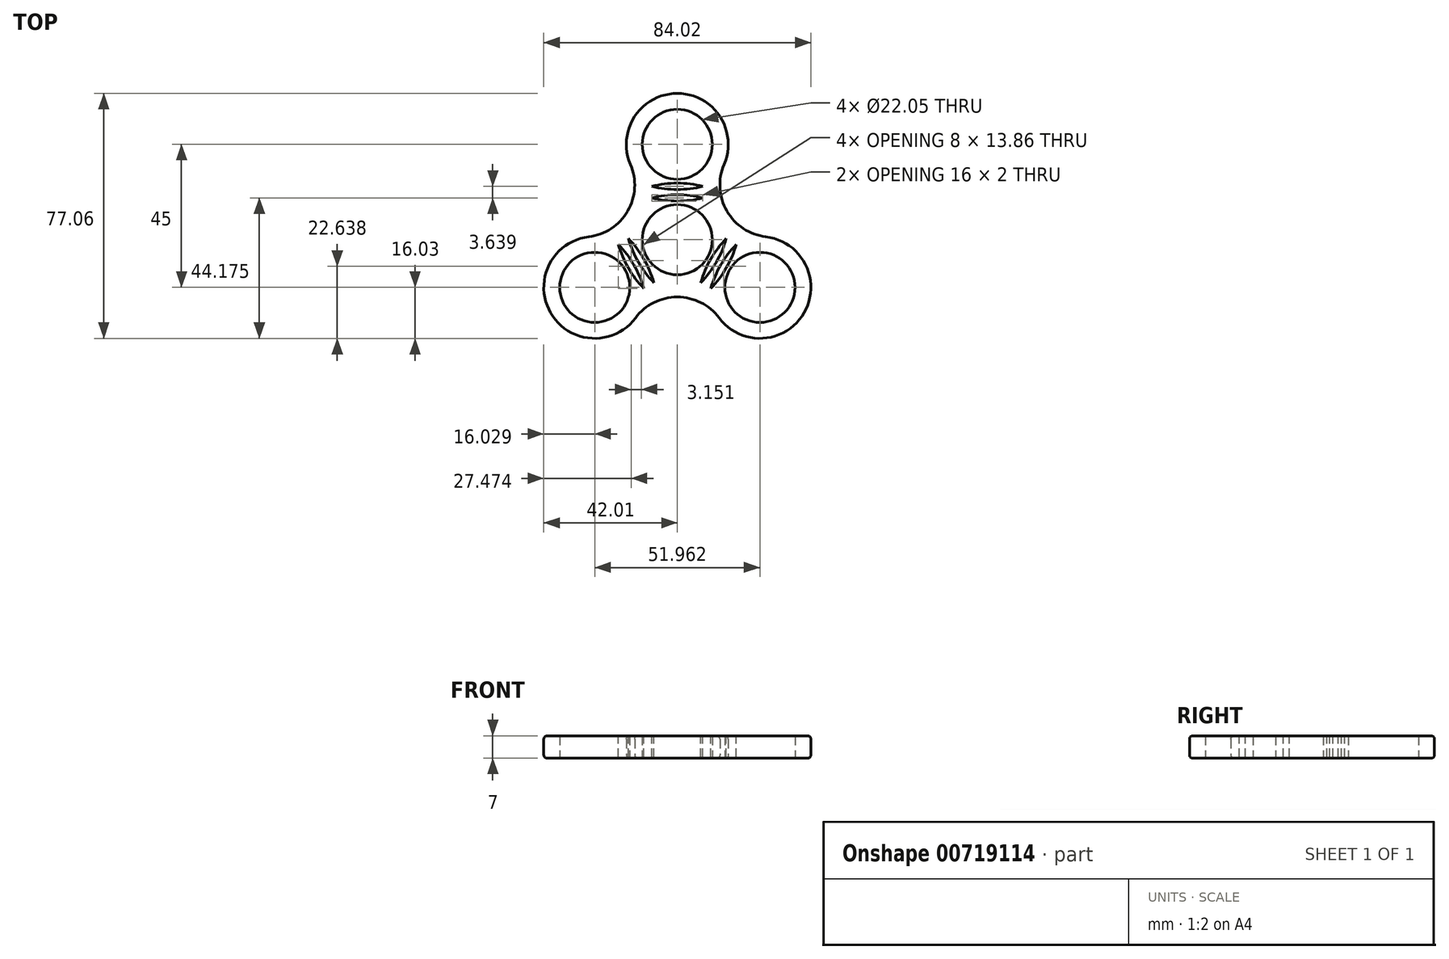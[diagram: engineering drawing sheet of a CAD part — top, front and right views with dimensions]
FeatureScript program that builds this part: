
annotation { "Feature Type Name" : "Feature", "Feature Type Description" : "" }
export const myFeature = defineFeature(function(context is Context, id is Id, definition is map)
    precondition{}
    {
        {
            var Q0;
            Q0=qCreatedBy(makeId("Top.planeOp"),FACE);
            var sketch = newSketch(context, id + "F0", { "sketchPlane" : qUnion([Q0])});
            skCircle(sketch, "E0", {"center": v(0, 0) * mm, "radius": 11.03 * mm});
            skCircle(sketch, "E1", {"center": v(0, 30) * mm, "radius": 11.03 * mm});
            skCircle(sketch, "E2.0", {"center": v(0, 30) * mm, "radius": 16.02 * mm});
            skCircle(sketch, "E3.0", {"center": v(0, 0) * mm, "radius": 18.02 * mm});
            skArc(sketch, "E4", {"start": v(-15.59, 9.05) * mm, "mid": v(-13.42, 16.25) * mm, "end": v(-14.72, 23.66) * mm});
            skLineSegment(sketch, "E5", {"start": v(0, -22.67) * mm, "end": v(0, 73.3) * mm, "construction": true});
            skArc(sketch, "E6.MirrorCS", {"start": v(15.59, 9.05) * mm, "mid": v(13.42, 16.25) * mm, "end": v(14.72, 23.66) * mm});
            skArc(sketch, "E7.1.0", {"start": v(-0.04, -18.02) * mm, "mid": v(-7.36, -19.75) * mm, "end": v(-13.13, -24.58) * mm});
            skArc(sketch, "E7.1.1", {"start": v(-15.63, 8.98) * mm, "mid": v(-20.78, 3.5) * mm, "end": v(-27.85, 0.92) * mm});
            skCircle(sketch, "E7.1.2", {"center": v(-25.98, -15) * mm, "radius": 16.02 * mm});
            skCircle(sketch, "E7.1.3", {"center": v(-25.98, -15) * mm, "radius": 11.03 * mm});
            skArc(sketch, "E7.2.0", {"start": v(15.63, 8.98) * mm, "mid": v(20.78, 3.5) * mm, "end": v(27.85, 0.92) * mm});
            skArc(sketch, "E7.2.1", {"start": v(0.04, -18.02) * mm, "mid": v(7.36, -19.75) * mm, "end": v(13.13, -24.58) * mm});
            skCircle(sketch, "E7.2.2", {"center": v(25.98, -15) * mm, "radius": 16.02 * mm});
            skCircle(sketch, "E7.2.3", {"center": v(25.98, -15) * mm, "radius": 11.03 * mm});
            skSolve(sketch);
        }
        {
            var Q0;
            Q0=qSketchRegion(id+"F0",true);
            var Q1;
            Q1=makeQuery(id+"F0.imprint","IMPRINT",FACE,{"disambiguationData":[TD([[makeQuery(id+"F0.imprint","IMPRINT",EDGE,{"derivedFrom":sQuery(id+"F0.wireOp",EDGE,"E0")}),-1.0]])]});
            var Q2;
            {var subQ0=sQuery(id+"F0.wireOp",EDGE,"E7.1.2");var subQ1=sQuery(id+"F0.wireOp",EDGE,"E3.0");var subQ2=makeQuery(id+"F0.imprint","INTERSECT",VERTEX,{"disambiguationData":[OD(0.0)],"derivedFrom":[subQ1,subQ0]});Q2=makeQuery(id+"F0.imprint","IMPRINT",FACE,{"disambiguationData":[TD([[makeQuery(id+"F0.imprint","IMPRINT",EDGE,{"disambiguationData":[TD([[subQ2,-1.0]])],"derivedFrom":subQ1}),1.0]])]});}
            var Q3;
            {var subQ0=sQuery(id+"F0.wireOp",EDGE,"E3.0");var subQ1=sQuery(id+"F0.wireOp",EDGE,"E2.0");var subQ2=makeQuery(id+"F0.imprint","INTERSECT",VERTEX,{"disambiguationData":[OD(0.0)],"derivedFrom":[subQ1,subQ0]});Q3=makeQuery(id+"F0.imprint","IMPRINT",FACE,{"disambiguationData":[TD([[makeQuery(id+"F0.imprint","IMPRINT",EDGE,{"disambiguationData":[TD([[subQ2,-1.0]])],"derivedFrom":subQ1}),1.0]])]});}
            var Q4;
            {var subQ0=sQuery(id+"F0.wireOp",EDGE,"E7.2.2");var subQ1=sQuery(id+"F0.wireOp",EDGE,"E3.0");var subQ2=makeQuery(id+"F0.imprint","INTERSECT",VERTEX,{"disambiguationData":[OD(0.0)],"derivedFrom":[subQ1,subQ0]});Q4=makeQuery(id+"F0.imprint","IMPRINT",FACE,{"disambiguationData":[TD([[makeQuery(id+"F0.imprint","IMPRINT",EDGE,{"disambiguationData":[TD([[subQ2,-1.0]])],"derivedFrom":subQ1}),1.0]])]});}
            extrude(context, id + "F1", {"entities" : qUnion([Q0, Q1, Q2, Q3, Q4]), "depth" : 7 * mm, "offsetDistance" : 25 * mm});
        }
        {
            var Q0;
            Q0=makeQuery(id+"F1.opExtrude","SWEPT_FACE",FACE,{"disambiguationData":[OSD([sQuery(id+"F0.wireOp",EDGE,"E2.0")])]});
            var Q1;
            Q1=makeQuery(id+"F1.opExtrude","SWEPT_FACE",FACE,{"disambiguationData":[OSD([sQuery(id+"F0.wireOp",EDGE,"E4")])]});
            var Q2;
            Q2=makeQuery(id+"F1.opExtrude","SWEPT_FACE",FACE,{"disambiguationData":[OSD([sQuery(id+"F0.wireOp",EDGE,"E7.1.1")])]});
            var Q3;
            Q3=makeQuery(id+"F1.opExtrude","SWEPT_FACE",FACE,{"disambiguationData":[OSD([sQuery(id+"F0.wireOp",EDGE,"E7.1.2")])]});
            var Q4;
            Q4=makeQuery(id+"F1.opExtrude","SWEPT_FACE",FACE,{"disambiguationData":[OSD([sQuery(id+"F0.wireOp",EDGE,"E7.2.1")])]});
            fillet(context, id + "F2", {"entities" : qUnion([Q0, Q1, Q2, Q3, Q4]), "radius" : 1 * mm, "tangentPropagation" : true, "allowEdgeOverflow" : false});
        }
        {
            var Q0;
            Q0=makeQuery(id+"F1.opExtrude","CAP_FACE",FACE,{"disambiguationData":[OSD([sQuery(id+"F0.wireOp",EDGE,"E0"),sQuery(id+"F0.wireOp",EDGE,"E1"),sQuery(id+"F0.wireOp",EDGE,"E2.0"),sQuery(id+"F0.wireOp",EDGE,"E3.0"),sQuery(id+"F0.wireOp",EDGE,"E4"),sQuery(id+"F0.wireOp",EDGE,"E6.MirrorCS"),sQuery(id+"F0.wireOp",EDGE,"E7.1.0"),sQuery(id+"F0.wireOp",EDGE,"E7.1.1"),sQuery(id+"F0.wireOp",EDGE,"E7.1.2"),sQuery(id+"F0.wireOp",EDGE,"E7.1.3"),sQuery(id+"F0.wireOp",EDGE,"E7.2.0"),sQuery(id+"F0.wireOp",EDGE,"E7.2.1"),sQuery(id+"F0.wireOp",EDGE,"E7.2.2"),sQuery(id+"F0.wireOp",EDGE,"E7.2.3")])],"isStart":false});
            var sketch = newSketch(context, id + "F3", { "sketchPlane" : qUnion([Q0])});
            skArc(sketch, "E8", {"start": v(8, 16.78) * mm, "mid": v(0, 17.78) * mm, "end": v(-8, 16.78) * mm});
            skArc(sketch, "E9", {"start": v(-8, 16.78) * mm, "mid": v(0, 15.79) * mm, "end": v(8, 16.78) * mm});
            skLineSegment(sketch, "E10", {"start": v(0, 48.36) * mm, "end": v(0, -14.8) * mm, "construction": true});
            skPoint(sketch, "E11", {"position": v(0, 17.78) * mm});
            skLineSegment(sketch, "E12", {"start": v(-8, 16.78) * mm, "end": v(-8, 48.36) * mm, "construction": true});
            skLineSegment(sketch, "E13", {"start": v(-8, 16.78) * mm, "end": v(-8, -14.8) * mm, "construction": true});
            skArc(sketch, "E14", {"start": v(8, 13.15) * mm, "mid": v(0, 14.14) * mm, "end": v(-8, 13.15) * mm});
            skArc(sketch, "E15", {"start": v(-8, 13.15) * mm, "mid": v(0, 12.15) * mm, "end": v(8, 13.15) * mm});
            skLineSegment(sketch, "E16", {"start": v(0, 44.72) * mm, "end": v(0, -18.43) * mm, "construction": true});
            skLineSegment(sketch, "E17", {"start": v(-8, 13.15) * mm, "end": v(-8, 44.72) * mm, "construction": true});
            skLineSegment(sketch, "E18", {"start": v(-8, 13.15) * mm, "end": v(-8, -18.43) * mm, "construction": true});
            skArc(sketch, "E19.1.0", {"start": v(-7.38, -13.5) * mm, "mid": v(-10.52, -6.07) * mm, "end": v(-15.38, 0.36) * mm});
            skArc(sketch, "E19.1.1", {"start": v(-15.38, 0.36) * mm, "mid": v(-12.25, -7.07) * mm, "end": v(-7.38, -13.5) * mm});
            skArc(sketch, "E19.1.2", {"start": v(-10.54, -15.32) * mm, "mid": v(-13.67, -7.9) * mm, "end": v(-18.54, -1.46) * mm});
            skArc(sketch, "E19.1.3", {"start": v(-18.54, -1.46) * mm, "mid": v(-15.4, -8.9) * mm, "end": v(-10.54, -15.32) * mm});
            skArc(sketch, "E19.2.0", {"start": v(15.38, 0.36) * mm, "mid": v(10.52, -6.07) * mm, "end": v(7.38, -13.5) * mm});
            skArc(sketch, "E19.2.1", {"start": v(7.38, -13.5) * mm, "mid": v(12.25, -7.07) * mm, "end": v(15.38, 0.36) * mm});
            skArc(sketch, "E19.2.2", {"start": v(18.54, -1.46) * mm, "mid": v(13.67, -7.9) * mm, "end": v(10.54, -15.32) * mm});
            skArc(sketch, "E19.2.3", {"start": v(10.54, -15.32) * mm, "mid": v(15.4, -8.9) * mm, "end": v(18.54, -1.46) * mm});
            skPoint(sketch, "E19.center", {"position": v(0, 0) * mm});
            skPoint(sketch, "E20", {"position": v(0, 45.02) * mm});
            skSolve(sketch);
        }
        {
            var Q0;
            Q0 = qSketchRegion(id + "F3", true);
            extrude(context, id + "F4", {"entities" : qUnion([Q0]), "operationType" : NewBodyOperationType.REMOVE, "oppositeDirection" : true, "depth" : 25 * mm, "offsetDistance" : 25 * mm});
        }
    });
